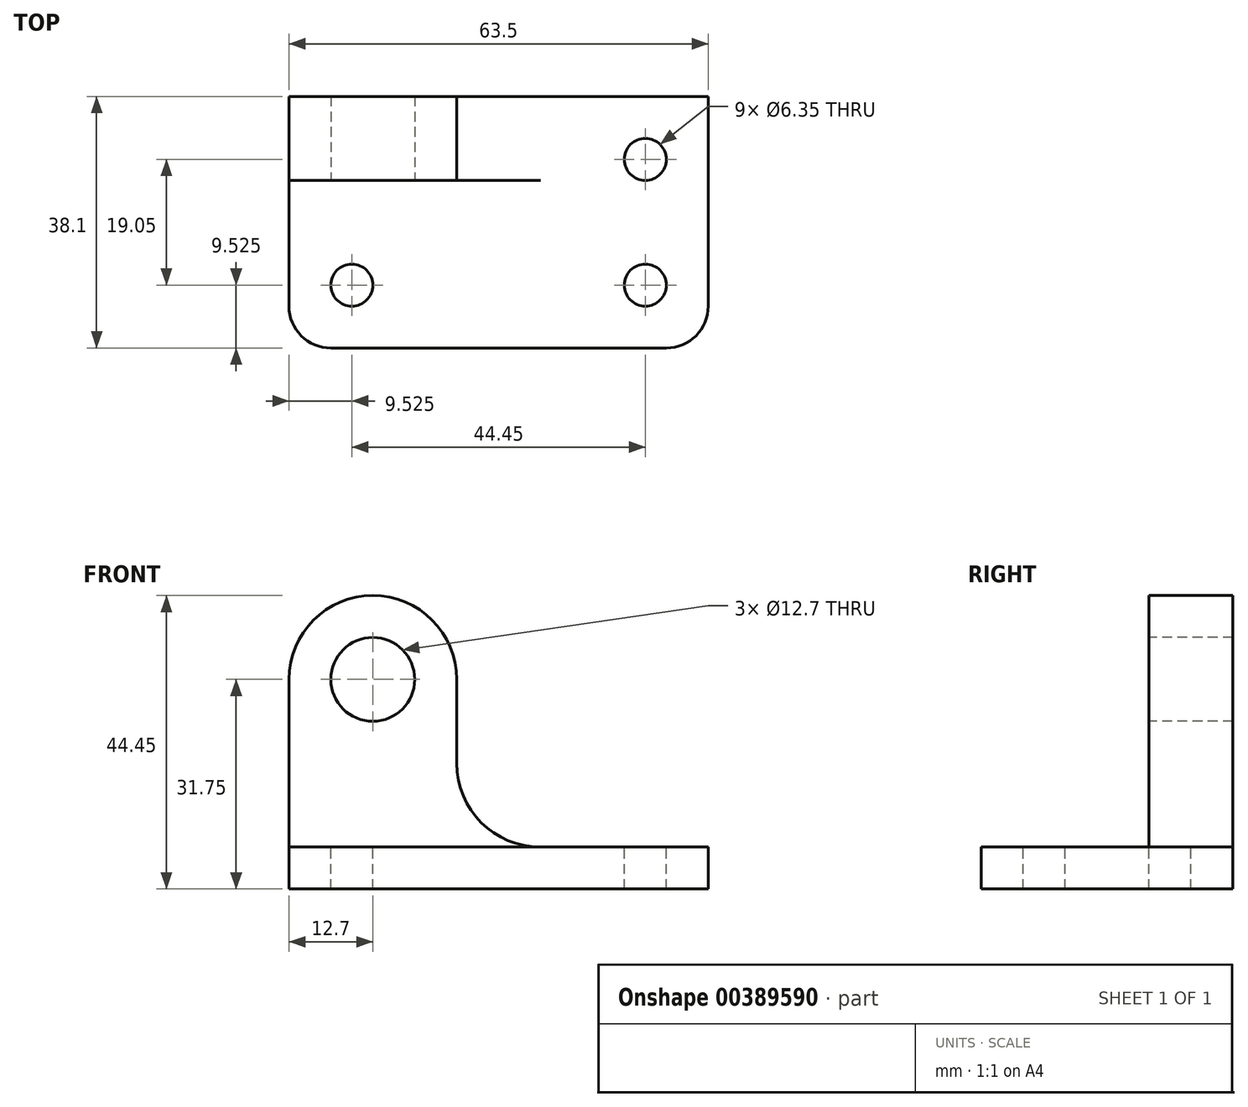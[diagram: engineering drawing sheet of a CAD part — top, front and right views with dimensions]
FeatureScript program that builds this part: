
annotation { "Feature Type Name" : "Feature", "Feature Type Description" : "" }
export const myFeature = defineFeature(function(context is Context, id is Id, definition is map)
    precondition{}
    {
        {
            var Q0;
            Q0=qCreatedBy(makeId("Front.planeOp"),FACE);
            var sketch = newSketch(context, id + "F0", { "sketchPlane" : qUnion([Q0])});
            skLineSegment(sketch, "E0.bottom", {"start": v(0, 44.45) * mm, "end": v(63.5, 44.45) * mm});
            skLineSegment(sketch, "E0.top", {"start": v(0, 0) * mm, "end": v(63.5, 0) * mm});
            skLineSegment(sketch, "E0.left", {"start": v(0, 44.45) * mm, "end": v(0, 0) * mm});
            skLineSegment(sketch, "E0.right", {"start": v(63.5, 44.45) * mm, "end": v(63.5, 0) * mm});
            skSolve(sketch);
        }
        {
            var Q0;
            Q0=makeQuery(id+"F0.imprint","IMPRINT",FACE,{"disambiguationData":[TD([[makeQuery(id+"F0.imprint","IMPRINT",EDGE,{"derivedFrom":sQuery(id+"F0.wireOp",EDGE,"E0.bottom")}),-1.0]])]});
            extrude(context, id + "F1", {"entities" : qUnion([Q0]), "depth" : 38.1 * mm});
        }
        {
            var Q0;
            Q0=makeQuery(id+"F1.opExtrude","CAP_FACE",FACE,{"disambiguationData":[OSD([sQuery(id+"F0.wireOp",EDGE,"E0.bottom"),sQuery(id+"F0.wireOp",EDGE,"E0.top"),sQuery(id+"F0.wireOp",EDGE,"E0.left"),sQuery(id+"F0.wireOp",EDGE,"E0.right")])],"isStart":false});
            var sketch = newSketch(context, id + "F2", { "sketchPlane" : qUnion([Q0])});
            skLineSegment(sketch, "E1", {"start": v(0, 6.35) * mm, "end": v(63.5, 6.35) * mm});
            skSolve(sketch);
        }
        {
            var Q0;
            {var subQ0=sQuery(id+"F2.wireOp",EDGE,"E1");Q0=makeQuery(id+"F2.imprint","IMPRINT",FACE,{"disambiguationData":[TD([[makeQuery(id+"F2.imprint","IMPRINT",EDGE,{"derivedFrom":subQ0}),1.0]])]});}
            extrude(context, id + "F3", {"entities" : qUnion([Q0]), "operationType" : NewBodyOperationType.REMOVE, "oppositeDirection" : true, "depth" : 25.4 * mm});
        }
        {
            var Q0;
            Q0=makeQuery(id+"F3.boolean.opBoolean","COPY",FACE,{"derivedFrom":makeQuery(id+"F3.opExtrude","CAP_FACE",FACE,{"disambiguationData":[OSD([sQuery(id+"F0.wireOp",EDGE,"E0.bottom"),sQuery(id+"F0.wireOp",EDGE,"E0.left"),sQuery(id+"F0.wireOp",EDGE,"E0.right"),sQuery(id+"F2.wireOp",EDGE,"E1")])],"isStart":false})});
            var sketch = newSketch(context, id + "F4", { "sketchPlane" : qUnion([Q0])});
            skLineSegment(sketch, "E2", {"start": v(0, 6.35) * mm, "end": v(0, 31.75) * mm});
            skLineSegment(sketch, "E3", {"start": v(12.7, 44.45) * mm, "end": v(12.7, 44.45) * mm});
            skLineSegment(sketch, "E4", {"start": v(25.4, 31.75) * mm, "end": v(25.4, 19.05) * mm});
            skLineSegment(sketch, "E5", {"start": v(38.1, 6.35) * mm, "end": v(63.5, 6.35) * mm});
            skPoint(sketch, "E6.visualSharp", {"position": v(25.4, 6.35) * mm});
            skArc(sketch, "E6.filletArc", {"start": v(25.4, 19.05) * mm, "mid": v(29.12, 10.07) * mm, "end": v(38.1, 6.35) * mm});
            skPoint(sketch, "E7.visualSharp", {"position": v(25.4, 44.45) * mm});
            skArc(sketch, "E7.filletArc", {"start": v(25.4, 31.75) * mm, "mid": v(21.68, 40.73) * mm, "end": v(12.7, 44.45) * mm});
            skPoint(sketch, "E8.visualSharp", {"position": v(0, 44.45) * mm});
            skArc(sketch, "E8.filletArc", {"start": v(12.7, 44.45) * mm, "mid": v(3.72, 40.73) * mm, "end": v(0, 31.75) * mm});
            skCircle(sketch, "E9", {"center": v(12.7, 31.75) * mm, "radius": 6.35 * mm});
            skSolve(sketch);
        }
        {
            var Q0;
            Q0=makeQuery(id+"F4.imprint","IMPRINT",FACE,{"disambiguationData":[TD([[makeQuery(id+"F4.imprint","IMPRINT",EDGE,{"derivedFrom":sQuery(id+"F4.wireOp",EDGE,"E4")}),1.0]])]});
            var Q1;
            Q1=makeQuery(id+"F4.imprint","IMPRINT",FACE,{"disambiguationData":[TD([[makeQuery(id+"F4.imprint","IMPRINT",EDGE,{"derivedFrom":sQuery(id+"F4.wireOp",EDGE,"E9")}),1.0]])]});
            var Q2;
            {var subQ0=sQuery(id+"F4.wireOp",EDGE,"E8.filletArc");Q2=makeQuery(id+"F4.imprint","IMPRINT",FACE,{"disambiguationData":[TD([[makeQuery(id+"F4.imprint","IMPRINT",EDGE,{"derivedFrom":subQ0}),-1.0]])]});}
            extrude(context, id + "F5", {"entities" : qUnion([Q0, Q1, Q2]), "operationType" : NewBodyOperationType.REMOVE, "oppositeDirection" : true, "depth" : 25.4 * mm});
        }
        {
            var Q0;
            Q0=makeQuery(id+"F5.boolean.opBoolean","MERGE",FACE,{"derivedFrom":[makeQuery(id+"F3.boolean.opBoolean","COPY",FACE,{"derivedFrom":makeQuery(id+"F3.opExtrude","SWEPT_FACE",FACE,{"disambiguationData":[OSD([sQuery(id+"F2.wireOp",EDGE,"E1")])]})}),makeQuery(id+"F5.opExtrude","SWEPT_FACE",FACE,{"disambiguationData":[OSD([sQuery(id+"F4.wireOp",EDGE,"E5")])]})]});
            var sketch = newSketch(context, id + "F6", { "sketchPlane" : qUnion([Q0])});
            skLineSegment(sketch, "E10", {"start": v(0, -12.7) * mm, "end": v(0, -31.75) * mm});
            skLineSegment(sketch, "E11", {"start": v(6.35, -38.1) * mm, "end": v(57.15, -38.1) * mm});
            skLineSegment(sketch, "E12", {"start": v(63.5, -31.75) * mm, "end": v(63.5, 0) * mm});
            skPoint(sketch, "E13.visualSharp", {"position": v(0, -38.1) * mm});
            skArc(sketch, "E13.filletArc", {"start": v(0, -31.75) * mm, "mid": v(1.86, -36.24) * mm, "end": v(6.35, -38.1) * mm});
            skPoint(sketch, "E14.visualSharp", {"position": v(63.5, -38.1) * mm});
            skArc(sketch, "E14.filletArc", {"start": v(57.15, -38.1) * mm, "mid": v(61.64, -36.24) * mm, "end": v(63.5, -31.75) * mm});
            skCircle(sketch, "E15", {"center": v(9.53, -28.58) * mm, "radius": 3.18 * mm});
            skCircle(sketch, "E16", {"center": v(53.98, -28.58) * mm, "radius": 3.18 * mm});
            skCircle(sketch, "E17", {"center": v(53.98, -9.53) * mm, "radius": 3.18 * mm});
            skSolve(sketch);
        }
        {
            var Q0;
            {var subQ0=sQuery(id+"F6.wireOp",EDGE,"E13.filletArc");Q0=makeQuery(id+"F6.imprint","IMPRINT",FACE,{"disambiguationData":[TD([[makeQuery(id+"F6.imprint","IMPRINT",EDGE,{"derivedFrom":subQ0}),-1.0]])]});}
            var Q1;
            Q1=makeQuery(id+"F6.imprint","IMPRINT",FACE,{"disambiguationData":[TD([[makeQuery(id+"F6.imprint","IMPRINT",EDGE,{"derivedFrom":sQuery(id+"F6.wireOp",EDGE,"E15")}),1.0]])]});
            var Q2;
            Q2=makeQuery(id+"F6.imprint","IMPRINT",FACE,{"disambiguationData":[TD([[makeQuery(id+"F6.imprint","IMPRINT",EDGE,{"derivedFrom":sQuery(id+"F6.wireOp",EDGE,"E16")}),1.0]])]});
            var Q3;
            {var subQ0=sQuery(id+"F6.wireOp",EDGE,"E14.filletArc");Q3=makeQuery(id+"F6.imprint","IMPRINT",FACE,{"disambiguationData":[TD([[makeQuery(id+"F6.imprint","IMPRINT",EDGE,{"derivedFrom":subQ0}),-1.0]])]});}
            var Q4;
            Q4=makeQuery(id+"F6.imprint","IMPRINT",FACE,{"disambiguationData":[TD([[makeQuery(id+"F6.imprint","IMPRINT",EDGE,{"derivedFrom":sQuery(id+"F6.wireOp",EDGE,"E17")}),1.0]])]});
            extrude(context, id + "F7", {"entities" : qUnion([Q0, Q1, Q2, Q3, Q4]), "operationType" : NewBodyOperationType.REMOVE, "oppositeDirection" : true, "depth" : 25.4 * mm});
        }
    });
